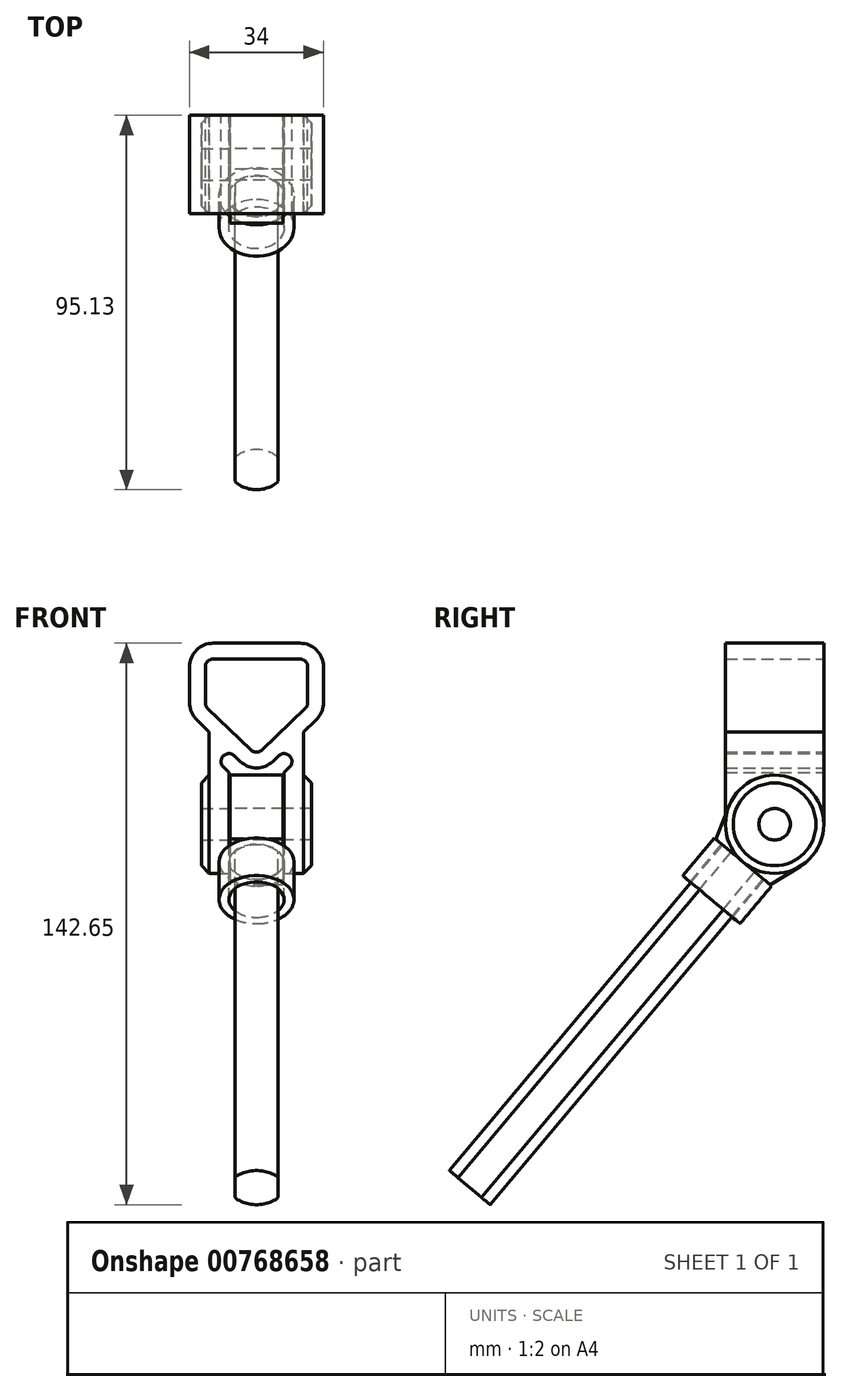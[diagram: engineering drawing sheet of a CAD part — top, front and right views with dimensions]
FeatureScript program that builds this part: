
annotation { "Feature Type Name" : "Feature", "Feature Type Description" : "" }
export const myFeature = defineFeature(function(context is Context, id is Id, definition is map)
    precondition{}
    {
        {
            var Q0;
            Q0=qCreatedBy(makeId("Front.planeOp"),FACE);
            var sketch = newSketch(context, id + "F0", { "sketchPlane" : qUnion([Q0])});
            skLineSegment(sketch, "E0", {"start": v(0, 42) * mm, "end": v(-11, 42) * mm});
            skLineSegment(sketch, "E1", {"start": v(-13, 40) * mm, "end": v(-13, 30.85) * mm});
            skLineSegment(sketch, "E2", {"start": v(-12.38, 29.4) * mm, "end": v(-1.38, 18.87) * mm});
            skLineSegment(sketch, "E3.MirrorCS", {"start": v(12.38, 29.4) * mm, "end": v(1.38, 18.87) * mm});
            skLineSegment(sketch, "E4.MirrorCS", {"start": v(0, 42) * mm, "end": v(11, 42) * mm});
            skLineSegment(sketch, "E5.MirrorCS", {"start": v(13, 40) * mm, "end": v(13, 30.85) * mm});
            skPoint(sketch, "E6.visualSharp", {"position": v(-13, 42) * mm});
            skArc(sketch, "E6.filletArc", {"start": v(-11, 42) * mm, "mid": v(-12.41, 41.41) * mm, "end": v(-13, 40) * mm});
            skPoint(sketch, "E7.visualSharp", {"position": v(13, 42) * mm});
            skArc(sketch, "E7.filletArc", {"start": v(13, 40) * mm, "mid": v(12.41, 41.41) * mm, "end": v(11, 42) * mm});
            skPoint(sketch, "E8.visualSharp", {"position": v(-13, 30) * mm});
            skArc(sketch, "E8.filletArc", {"start": v(-13, 30.85) * mm, "mid": v(-12.84, 30.07) * mm, "end": v(-12.38, 29.4) * mm});
            skPoint(sketch, "E9.visualSharp", {"position": v(13, 30) * mm});
            skArc(sketch, "E9.filletArc", {"start": v(12.38, 29.4) * mm, "mid": v(12.84, 30.07) * mm, "end": v(13, 30.85) * mm});
            skPoint(sketch, "E10.visualSharp", {"position": v(0, 17.55) * mm});
            skArc(sketch, "E10.filletArc", {"start": v(-1.38, 18.87) * mm, "mid": v(0, 18.32) * mm, "end": v(1.38, 18.87) * mm});
            skLineSegment(sketch, "E11.0", {"start": v(-15.15, 26.52) * mm, "end": v(-12, 23.5) * mm});
            skArc(sketch, "E11.1", {"start": v(-17, 30.85) * mm, "mid": v(-16.52, 28.5) * mm, "end": v(-15.15, 26.52) * mm});
            skLineSegment(sketch, "E11.2", {"start": v(-17, 40) * mm, "end": v(-17, 30.85) * mm});
            skArc(sketch, "E11.3", {"start": v(-11, 46) * mm, "mid": v(-15.24, 44.24) * mm, "end": v(-17, 40) * mm});
            skLineSegment(sketch, "E11.4", {"start": v(0, 46) * mm, "end": v(-11, 46) * mm});
            skArc(sketch, "E11.5", {"start": v(-4.15, 15.99) * mm, "mid": v(0, 14.32) * mm, "end": v(4.15, 15.99) * mm});
            skLineSegment(sketch, "E11.6", {"start": v(15.15, 26.52) * mm, "end": v(12, 23.5) * mm});
            skArc(sketch, "E11.7", {"start": v(15.15, 26.52) * mm, "mid": v(16.52, 28.5) * mm, "end": v(17, 30.85) * mm});
            skLineSegment(sketch, "E11.8", {"start": v(17, 40) * mm, "end": v(17, 30.85) * mm});
            skArc(sketch, "E11.9", {"start": v(17, 40) * mm, "mid": v(15.24, 44.24) * mm, "end": v(11, 46) * mm});
            skLineSegment(sketch, "E11.10", {"start": v(0, 46) * mm, "end": v(11, 46) * mm});
            skLineSegment(sketch, "E12", {"start": v(-12, -12.5) * mm, "end": v(-7, -12.5) * mm});
            skLineSegment(sketch, "E13", {"start": v(-7, -12.5) * mm, "end": v(-7, 13.18) * mm});
            skLineSegment(sketch, "E14.trimOffspring", {"start": v(-12, 23.5) * mm, "end": v(-12, -12.5) * mm});
            skArc(sketch, "E15", {"start": v(-5.62, 17.4) * mm, "mid": v(-8.44, 17.33) * mm, "end": v(-8.38, 14.5) * mm});
            skPoint(sketch, "E16", {"position": v(-5.62, 17.4) * mm});
            skPoint(sketch, "E17.MirrorCS.start.orphan", {"position": v(12, 23.5) * mm});
            skLineSegment(sketch, "E18", {"start": v(-8.38, 14.5) * mm, "end": v(-7, 13.18) * mm});
            skArc(sketch, "E19.MirrorCS", {"start": v(5.62, 17.4) * mm, "mid": v(8.44, 17.33) * mm, "end": v(8.38, 14.5) * mm});
            skLineSegment(sketch, "E20.MirrorCS", {"start": v(8.38, 14.5) * mm, "end": v(7, 13.18) * mm});
            skLineSegment(sketch, "E21.MirrorCS", {"start": v(7, -12.5) * mm, "end": v(7, 13.18) * mm});
            skLineSegment(sketch, "E22.MirrorCS", {"start": v(12, 23.5) * mm, "end": v(12, -12.5) * mm});
            skLineSegment(sketch, "E23.MirrorCS", {"start": v(12, -12.5) * mm, "end": v(7, -12.5) * mm});
            skLineSegment(sketch, "E24.trimOffspring", {"start": v(-5.62, 17.4) * mm, "end": v(-4.15, 15.99) * mm});
            skLineSegment(sketch, "E25.trimOffspring", {"start": v(5.62, 17.4) * mm, "end": v(4.15, 15.99) * mm});
            skSolve(sketch);
        }
        {
            var Q0;
            Q0 = qSketchRegion(id + "F0", true);
            extrude(context, id + "F1", {"entities" : qUnion([Q0]), "depth" : 25 * mm, "offsetDistance" : 25 * mm});
        }
        {
            var Q0;
            Q0=makeQuery(id+"F1.opExtrude","SWEPT_FACE",FACE,{"disambiguationData":[OSD([sQuery(id+"F0.wireOp",EDGE,"E22.MirrorCS")])]});
            var sketch = newSketch(context, id + "F2", { "sketchPlane" : qUnion([Q0])});
            skLineSegment(sketch, "E26", {"start": v(-33.45, 0) * mm, "end": v(7.24, 0) * mm, "construction": true});
            skLineSegment(sketch, "E27", {"start": v(-12.5, 12.5) * mm, "end": v(-12.5, -23.12) * mm, "construction": true});
            skCircle(sketch, "E28", {"center": v(-12.5, 0) * mm, "radius": 12.5 * mm});
            skCircle(sketch, "E29", {"center": v(-12.5, 0) * mm, "radius": 4 * mm});
            skSolve(sketch);
        }
        {
            var Q0;
            {var subQ0=sQuery(id+"F2.wireOp",EDGE,"E28");var subQ1=sQuery(id+"F0.wireOp",EDGE,"E22.MirrorCS");var subQ2=makeQuery(id+"F1.opExtrude","CAP_EDGE",EDGE,{"disambiguationData":[OSD([subQ1])],"isStart":false});var subQ3=makeQuery(id+"F2.imprint","INTERSECT",VERTEX,{"derivedFrom":[subQ2,subQ0]});Q0=makeQuery(id+"F2.imprint","IMPRINT",FACE,{"disambiguationData":[TD([[makeQuery(id+"F2.imprint","IMPRINT",EDGE,{"disambiguationData":[TD([[subQ3,-1.0]])],"derivedFrom":subQ0}),-1.0]])]});}
            var Q1;
            {var subQ0=sQuery(id+"F2.wireOp",EDGE,"E28");var subQ1=sQuery(id+"F0.wireOp",EDGE,"E22.MirrorCS");var subQ2=makeQuery(id+"F1.opExtrude","CAP_EDGE",EDGE,{"disambiguationData":[OSD([subQ1])],"isStart":true});var subQ3=makeQuery(id+"F2.imprint","INTERSECT",VERTEX,{"derivedFrom":[subQ2,subQ0]});Q1=makeQuery(id+"F2.imprint","IMPRINT",FACE,{"disambiguationData":[TD([[makeQuery(id+"F2.imprint","IMPRINT",EDGE,{"disambiguationData":[TD([[subQ3,1.0]])],"derivedFrom":subQ0}),-1.0]])]});}
            extrude(context, id + "F3", {"entities" : qUnion([Q0, Q1]), "operationType" : NewBodyOperationType.REMOVE, "oppositeDirection" : true, "depth" : 25 * mm, "offsetDistance" : 25 * mm});
        }
        {
            var Q0;
            Q0 = qSketchRegion(id + "F2", true);
            extrude(context, id + "F4", {"entities" : qUnion([Q0]), "operationType" : NewBodyOperationType.ADD, "depth" : 2 * mm, "offsetDistance" : 25 * mm});
        }
        {
            var Q0;
            Q0=makeQuery(id+"F4.opExtrude","CAP_EDGE",EDGE,{"disambiguationData":[OSD([sQuery(id+"F2.wireOp",EDGE,"E28")])],"isStart":false});
            chamfer(context, id + "F5", {"entities" : qUnion([Q0]), "width" : 2 * mm, "tangentPropagation" : true});
        }
        {
            var Q0;
            Q0=makeQuery(id+"F1.opExtrude","SWEPT_FACE",FACE,{"disambiguationData":[OSD([sQuery(id+"F0.wireOp",EDGE,"E14.trimOffspring")])]});
            var sketch = newSketch(context, id + "F6", { "sketchPlane" : qUnion([Q0])});
            skCircle(sketch, "E30", {"center": v(12.5, 0) * mm, "radius": 12.5 * mm});
            skSolve(sketch);
        }
        {
            var Q0;
            Q0 = qSketchRegion(id + "F6", true);
            extrude(context, id + "F7", {"entities" : qUnion([Q0]), "operationType" : NewBodyOperationType.ADD, "depth" : 2 * mm, "offsetDistance" : 25 * mm});
        }
        {
            var Q0;
            Q0=makeQuery(id+"F7.opExtrude","CAP_EDGE",EDGE,{"disambiguationData":[OSD([sQuery(id+"F6.wireOp",EDGE,"E30")])],"isStart":false});
            chamfer(context, id + "F8", {"entities" : qUnion([Q0]), "width" : 2 * mm, "tangentPropagation" : true});
        }
        {
            var Q0;
            Q0=makeQuery(id+"F2.imprint","IMPRINT",FACE,{"disambiguationData":[TD([[makeQuery(id+"F2.imprint","IMPRINT",EDGE,{"derivedFrom":sQuery(id+"F2.wireOp",EDGE,"E29")}),1.0]])]});
            extrude(context, id + "F9", {"entities" : qUnion([Q0]), "operationType" : NewBodyOperationType.REMOVE, "oppositeDirection" : true, "depth" : 30 * mm, "offsetDistance" : 25 * mm});
        }
        {
            var Q0;
            Q0=qCreatedBy(makeId("Right.planeOp"),FACE);
            var sketch = newSketch(context, id + "F10", { "sketchPlane" : qUnion([Q0])});
            skLineSegment(sketch, "E31", {"start": v(-12.5, 51.35) * mm, "end": v(-12.5, -23.85) * mm, "construction": true});
            skLineSegment(sketch, "E32", {"start": v(-12.5, 0) * mm, "end": v(-2.92, -8.03) * mm, "construction": true});
            skLineSegment(sketch, "E33", {"start": v(-2.92, -8.03) * mm, "end": v(-12.5, 0) * mm, "construction": true});
            skLineSegment(sketch, "E34", {"start": v(-22.08, 8.03) * mm, "end": v(-12.5, 0) * mm, "construction": true});
            skArc(sketch, "E35", {"start": v(-5.97, -10.66) * mm, "mid": v(-4.47, 9.58) * mm, "end": v(-24.13, 4.58) * mm});
            skCircle(sketch, "E36", {"center": v(-12.5, 0) * mm, "radius": 4 * mm});
            skLineSegment(sketch, "E37", {"start": v(-27.43, -3.8) * mm, "end": v(-20.53, -9.58) * mm});
            skLineSegment(sketch, "E38", {"start": v(-24.13, 4.58) * mm, "end": v(-27.43, -3.8) * mm});
            skPoint(sketch, "E39", {"position": v(-27.43, -3.8) * mm});
            skLineSegment(sketch, "E40.MirrorCS", {"start": v(-5.97, -10.66) * mm, "end": v(-13.64, -15.36) * mm});
            skLineSegment(sketch, "E41.MirrorCS", {"start": v(-13.64, -15.36) * mm, "end": v(-20.53, -9.58) * mm});
            skSolve(sketch);
        }
        {
            var Q0;
            Q0=makeQuery(id+"F10.imprint","IMPRINT",FACE,{"disambiguationData":[TD([[makeQuery(id+"F10.imprint","IMPRINT",EDGE,{"derivedFrom":sQuery(id+"F10.wireOp",EDGE,"E35")}),1.0]])]});
            extrude(context, id + "F11", {"entities" : qUnion([Q0]), "endBound" : BoundingType.SYMMETRIC, "depth" : 13.5 * mm, "offsetDistance" : 25 * mm});
        }
        {
            var Q0;
            Q0=makeQuery(id+"F11.opExtrude","SWEPT_FACE",FACE,{"disambiguationData":[OSD([sQuery(id+"F10.wireOp",EDGE,"E37"),sQuery(id+"F10.wireOp",EDGE,"E41.MirrorCS")])]});
            var sketch = newSketch(context, id + "F12", { "sketchPlane" : qUnion([Q0])});
            skLineSegment(sketch, "E42", {"start": v(6.75, 0.58) * mm, "end": v(-6.75, 18.58) * mm, "construction": true});
            skLineSegment(sketch, "E43", {"start": v(-6.75, 18.58) * mm, "end": v(6.75, 18.58) * mm, "construction": true});
            skLineSegment(sketch, "E44", {"start": v(6.75, 18.58) * mm, "end": v(-6.75, 0.58) * mm, "construction": true});
            skPoint(sketch, "E45", {"position": v(0, 9.58) * mm});
            skArc(sketch, "E46", {"start": v(5.5, 13.49) * mm, "mid": v(0, 16.33) * mm, "end": v(-5.5, 13.49) * mm});
            skLineSegment(sketch, "E47.trimOffspring", {"start": v(5.5, 5.66) * mm, "end": v(5.5, 13.49) * mm});
            skLineSegment(sketch, "E48.MirrorCS", {"start": v(-5.5, 5.66) * mm, "end": v(-5.5, 13.49) * mm});
            skArc(sketch, "E49.trimOffspring", {"start": v(-5.5, 5.66) * mm, "mid": v(0, 2.83) * mm, "end": v(5.5, 5.66) * mm});
            skCircle(sketch, "E50", {"center": v(0, 9.58) * mm, "radius": 7 * mm});
            skCircle(sketch, "E51", {"center": v(0, 9.58) * mm, "radius": 9.5 * mm});
            skSolve(sketch);
        }
        {
            var Q0;
            Q0=makeQuery(id+"F12.imprint","IMPRINT",FACE,{"disambiguationData":[TD([[makeQuery(id+"F12.imprint","IMPRINT",EDGE,{"derivedFrom":sQuery(id+"F12.wireOp",EDGE,"E46")}),1.0]])]});
            extrude(context, id + "F13", {"entities" : qUnion([Q0]), "operationType" : NewBodyOperationType.ADD, "depth" : 108 * mm, "offsetDistance" : 25 * mm});
        }
        {
            var Q0;
            Q0 = qSketchRegion(id + "F12", true);
            extrude(context, id + "F14", {"entities" : qUnion([Q0]), "depth" : 12.5 * mm, "offsetDistance" : 25 * mm});
        }
    });
